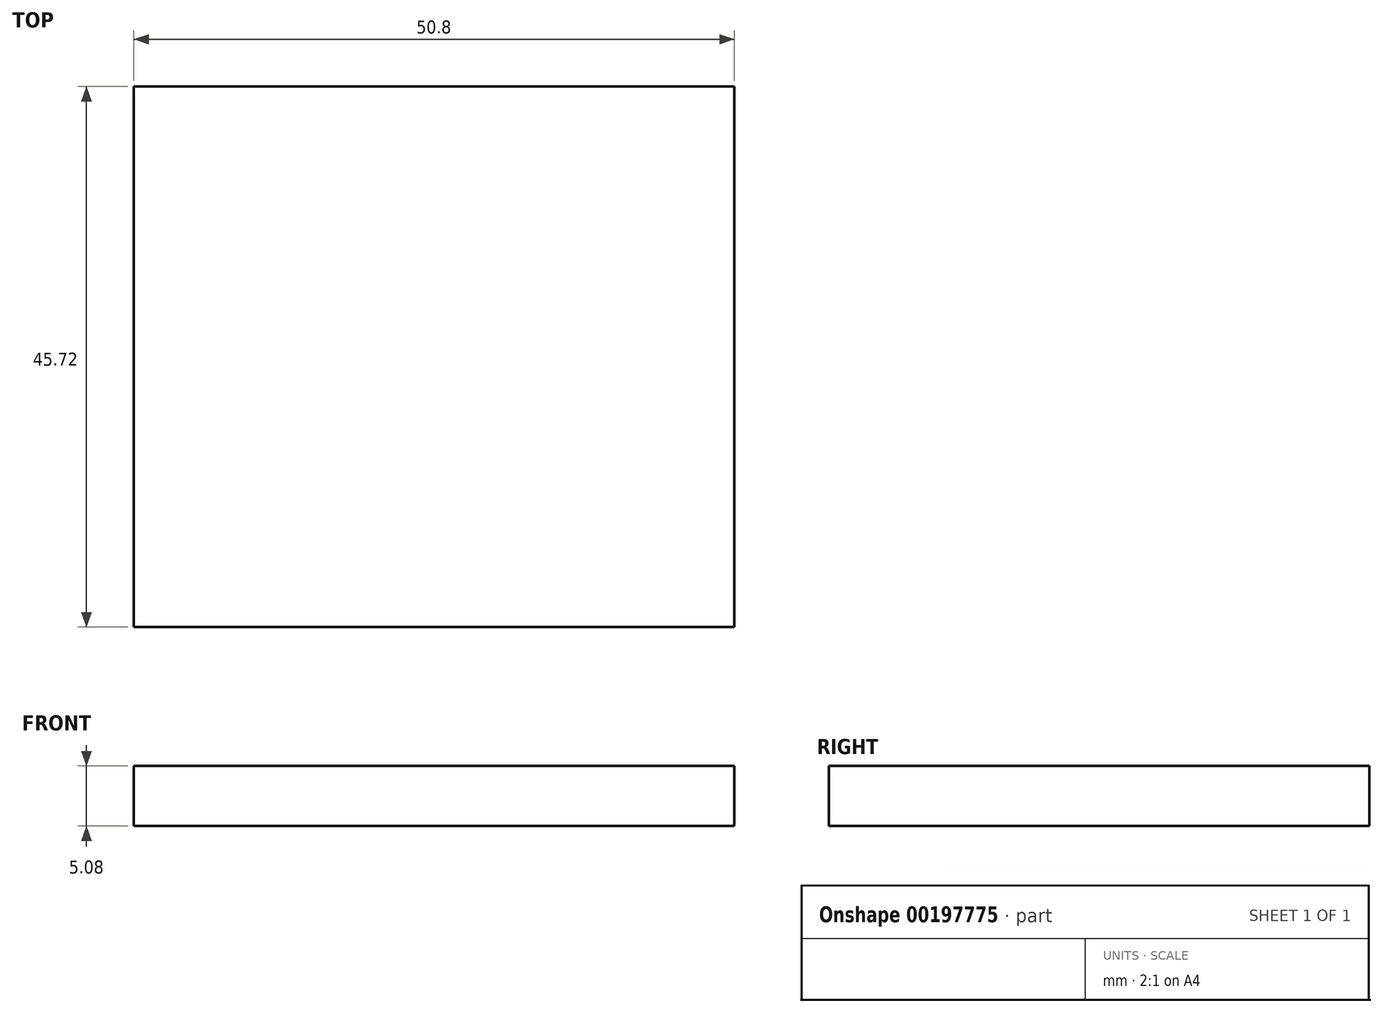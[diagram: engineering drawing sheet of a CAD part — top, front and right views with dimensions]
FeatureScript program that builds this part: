
annotation { "Feature Type Name" : "Feature", "Feature Type Description" : "" }
export const myFeature = defineFeature(function(context is Context, id is Id, definition is map)
    precondition{}
    {
        {
            var Q0;
            Q0=qCreatedBy(makeId("Top.planeOp"),FACE);
            var sketch = newSketch(context, id + "F0", { "sketchPlane" : qUnion([Q0])});
            skLineSegment(sketch, "E0.bottom", {"start": v(-25.4, 22.86) * mm, "end": v(25.4, 22.86) * mm});
            skLineSegment(sketch, "E0.top", {"start": v(-25.4, -22.86) * mm, "end": v(25.4, -22.86) * mm});
            skLineSegment(sketch, "E0.left", {"start": v(-25.4, 22.86) * mm, "end": v(-25.4, -22.86) * mm});
            skLineSegment(sketch, "E0.right", {"start": v(25.4, 22.86) * mm, "end": v(25.4, -22.86) * mm});
            skSolve(sketch);
        }
        {
            var Q0;
            Q0=makeQuery(id+"F0.imprint","IMPRINT",FACE,{"disambiguationData":[TD([[makeQuery(id+"F0.imprint","IMPRINT",EDGE,{"derivedFrom":sQuery(id+"F0.wireOp",EDGE,"E0.bottom")}),-1.0]])]});
            extrude(context, id + "F1", {"entities" : qUnion([Q0]), "depth" : 5.08 * mm});
        }
    });
